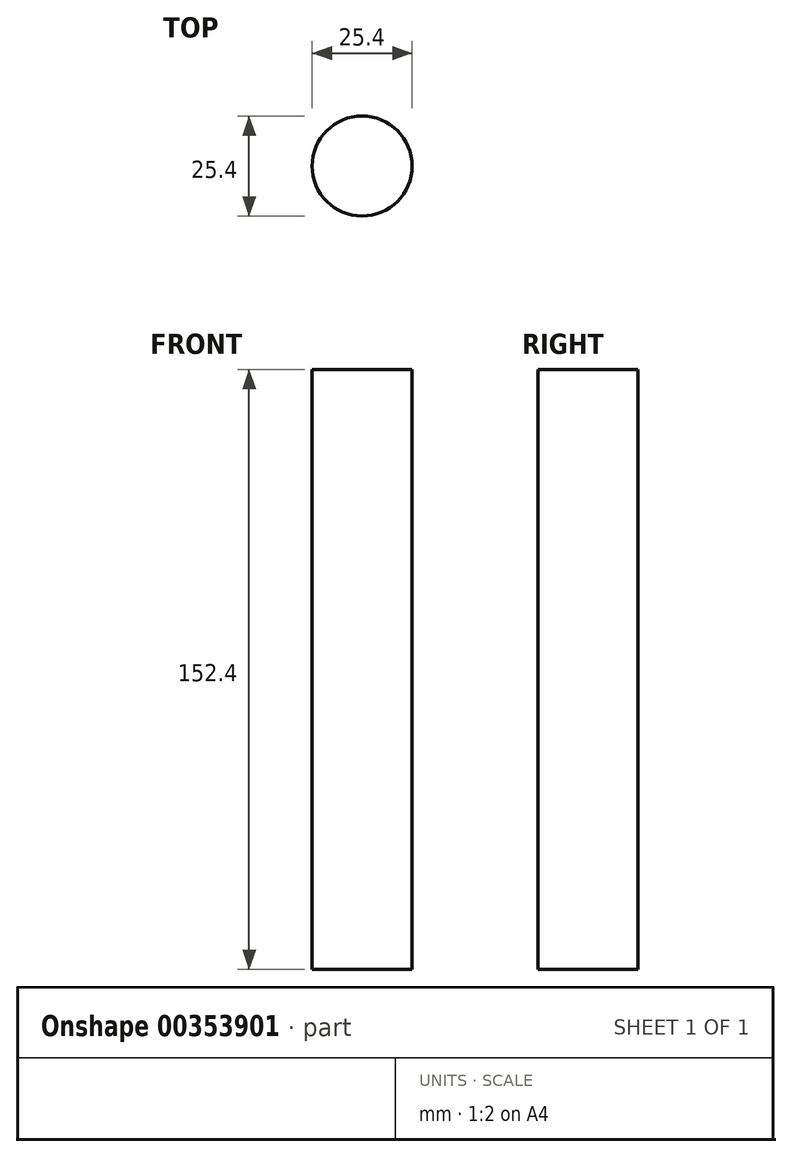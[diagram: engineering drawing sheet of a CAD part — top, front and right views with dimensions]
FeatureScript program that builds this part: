
annotation { "Feature Type Name" : "Feature", "Feature Type Description" : "" }
export const myFeature = defineFeature(function(context is Context, id is Id, definition is map)
    precondition{}
    {
        {
            var Q0;
            Q0=qCreatedBy(makeId("Top.planeOp"),FACE);
            var sketch = newSketch(context, id + "F0", { "sketchPlane" : qUnion([Q0])});
            skCircle(sketch, "E0", {"center": v(0, 0) * mm, "radius": 12.7 * mm});
            skSolve(sketch);
        }
        {
            var Q0;
            Q0 = qSketchRegion(id + "F0", true);
            extrude(context, id + "F1", {"entities" : qUnion([Q0]), "depth" : 152.4 * mm});
        }
    });
